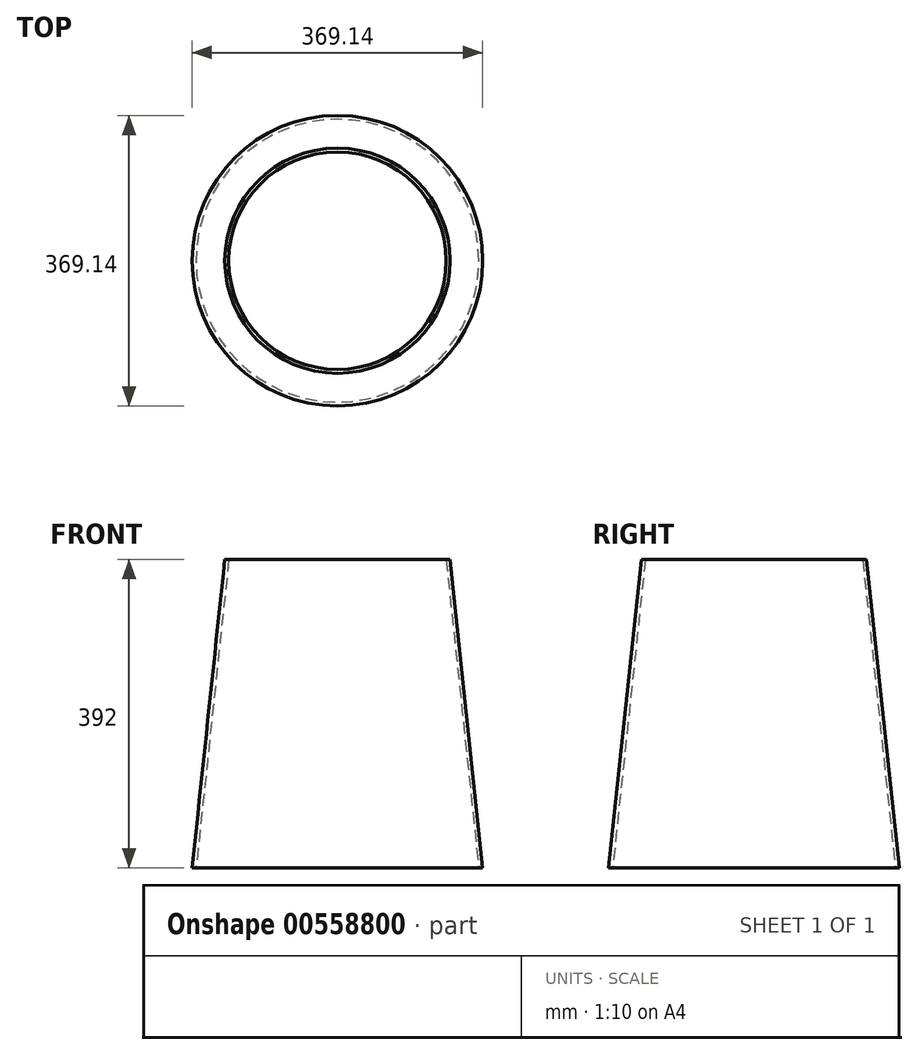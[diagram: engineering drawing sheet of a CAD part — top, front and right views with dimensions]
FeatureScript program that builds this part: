
annotation { "Feature Type Name" : "Feature", "Feature Type Description" : "" }
export const myFeature = defineFeature(function(context is Context, id is Id, definition is map)
    precondition{}
    {
        {
            var Q0;
            Q0=qCreatedBy(makeId("Front.planeOp"),FACE);
            var sketch = newSketch(context, id + "F0", { "sketchPlane" : qUnion([Q0])});
            skLineSegment(sketch, "E0", {"start": v(0, 0) * mm, "end": v(0, 500) * mm, "construction": true});
            skLineSegment(sketch, "E1", {"start": v(179.6, 58) * mm, "end": v(138.1, 449.47) * mm});
            skLineSegment(sketch, "E2", {"start": v(179.6, 58) * mm, "end": v(184.57, 58.53) * mm});
            skLineSegment(sketch, "E3", {"start": v(184.57, 58.53) * mm, "end": v(143.07, 450) * mm});
            skLineSegment(sketch, "E4", {"start": v(138.1, 449.47) * mm, "end": v(143.07, 450) * mm});
            skSolve(sketch);
        }
        {
            var Q0;
            Q0=makeQuery(id+"F0.imprint","IMPRINT",FACE,{"disambiguationData":[TD([[makeQuery(id+"F0.imprint","IMPRINT",EDGE,{"derivedFrom":sQuery(id+"F0.wireOp",EDGE,"E1")}),-1.0]])]});
            var Q1;
            Q1=sQuery(id+"F0.wireOp",EDGE,"E0");
            revolve(context, id + "F1", {"entities" : qUnion([Q0]), "axis" : qUnion([Q1]), "revolveType" : RevolveType.FULL});
        }
    });
